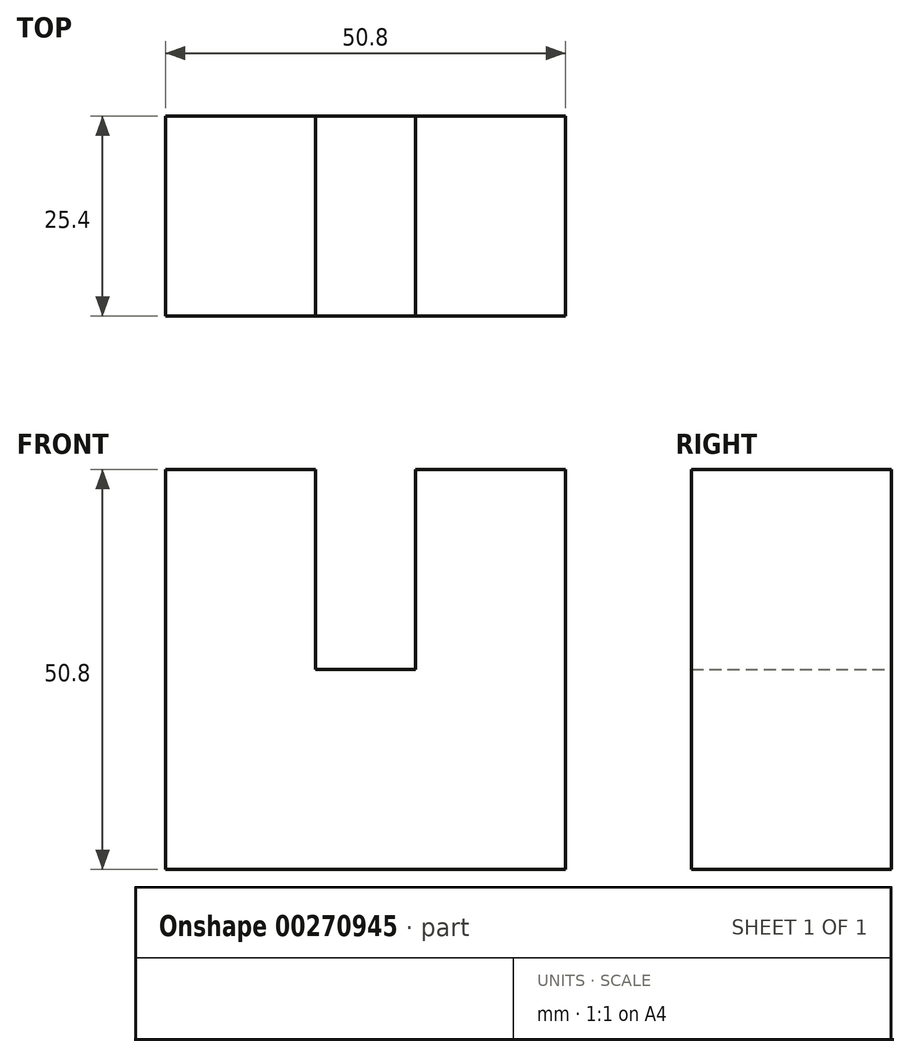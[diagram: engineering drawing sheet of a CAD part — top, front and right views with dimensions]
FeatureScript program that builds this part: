
annotation { "Feature Type Name" : "Feature", "Feature Type Description" : "" }
export const myFeature = defineFeature(function(context is Context, id is Id, definition is map)
    precondition{}
    {
        {
            var Q0;
            Q0=qCreatedBy(makeId("Front.planeOp"),FACE);
            var sketch = newSketch(context, id + "F0", { "sketchPlane" : qUnion([Q0])});
            skLineSegment(sketch, "E0", {"start": v(-63.21, 58.24) * mm, "end": v(-63.21, 7.44) * mm});
            skLineSegment(sketch, "E1", {"start": v(-63.21, 7.44) * mm, "end": v(-12.41, 7.44) * mm});
            skLineSegment(sketch, "E2", {"start": v(-12.41, 7.44) * mm, "end": v(-12.41, 58.24) * mm});
            skLineSegment(sketch, "E3", {"start": v(-63.21, 58.24) * mm, "end": v(-44.16, 58.24) * mm});
            skLineSegment(sketch, "E4", {"start": v(-12.41, 58.24) * mm, "end": v(-31.46, 58.24) * mm});
            skLineSegment(sketch, "E5", {"start": v(-31.46, 58.24) * mm, "end": v(-31.46, 32.84) * mm});
            skLineSegment(sketch, "E6", {"start": v(-44.16, 58.24) * mm, "end": v(-44.16, 32.84) * mm});
            skLineSegment(sketch, "E7", {"start": v(-44.16, 32.84) * mm, "end": v(-31.46, 32.84) * mm});
            skSolve(sketch);
        }
        {
            var Q0;
            Q0 = qSketchRegion(id + "F0", true);
            extrude(context, id + "F1", {"entities" : qUnion([Q0]), "depth" : 25.4 * mm});
        }
    });
